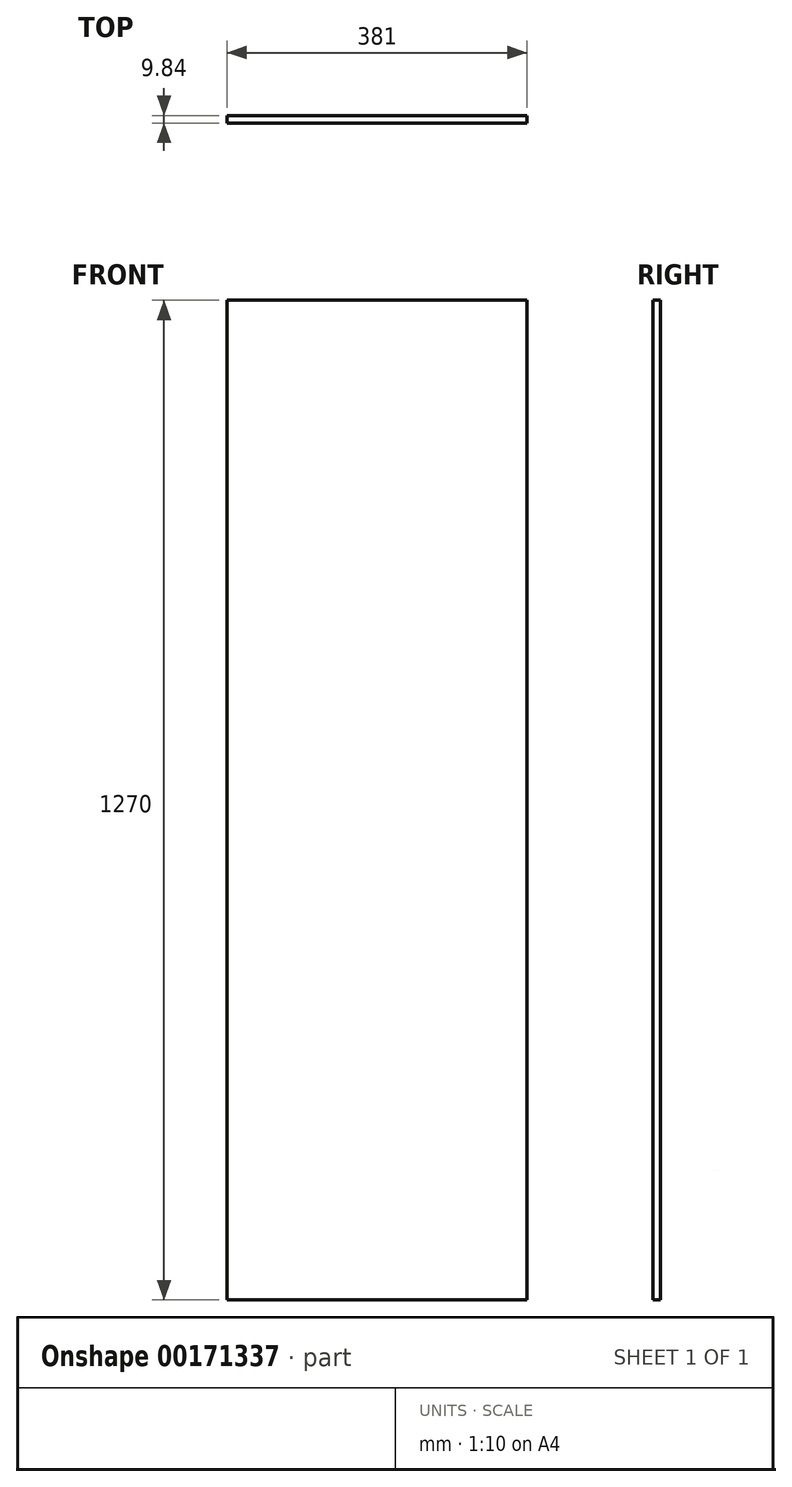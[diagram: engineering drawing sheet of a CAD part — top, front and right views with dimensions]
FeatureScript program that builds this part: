
annotation { "Feature Type Name" : "Feature", "Feature Type Description" : "" }
export const myFeature = defineFeature(function(context is Context, id is Id, definition is map)
    precondition{}
    {
        {
            var Q0;
            Q0=qCreatedBy(makeId("Front.planeOp"),FACE);
            var sketch = newSketch(context, id + "F0", { "sketchPlane" : qUnion([Q0])});
            skLineSegment(sketch, "E0.bottom", {"start": v(0, 0) * mm, "end": v(381, 0) * mm});
            skLineSegment(sketch, "E0.top", {"start": v(0, -1270) * mm, "end": v(381, -1270) * mm});
            skLineSegment(sketch, "E0.left", {"start": v(0, 0) * mm, "end": v(0, -1270) * mm});
            skLineSegment(sketch, "E0.right", {"start": v(381, 0) * mm, "end": v(381, -1270) * mm});
            skSolve(sketch);
        }
        {
            var Q0;
            Q0=makeQuery(id+"F0.imprint","IMPRINT",FACE,{"disambiguationData":[TD([[makeQuery(id+"F0.imprint","IMPRINT",EDGE,{"derivedFrom":sQuery(id+"F0.wireOp",EDGE,"E0.bottom")}),-1.0]])]});
            extrude(context, id + "F1", {"entities" : qUnion([Q0]), "depth" : 9.84 * mm});
        }
    });
